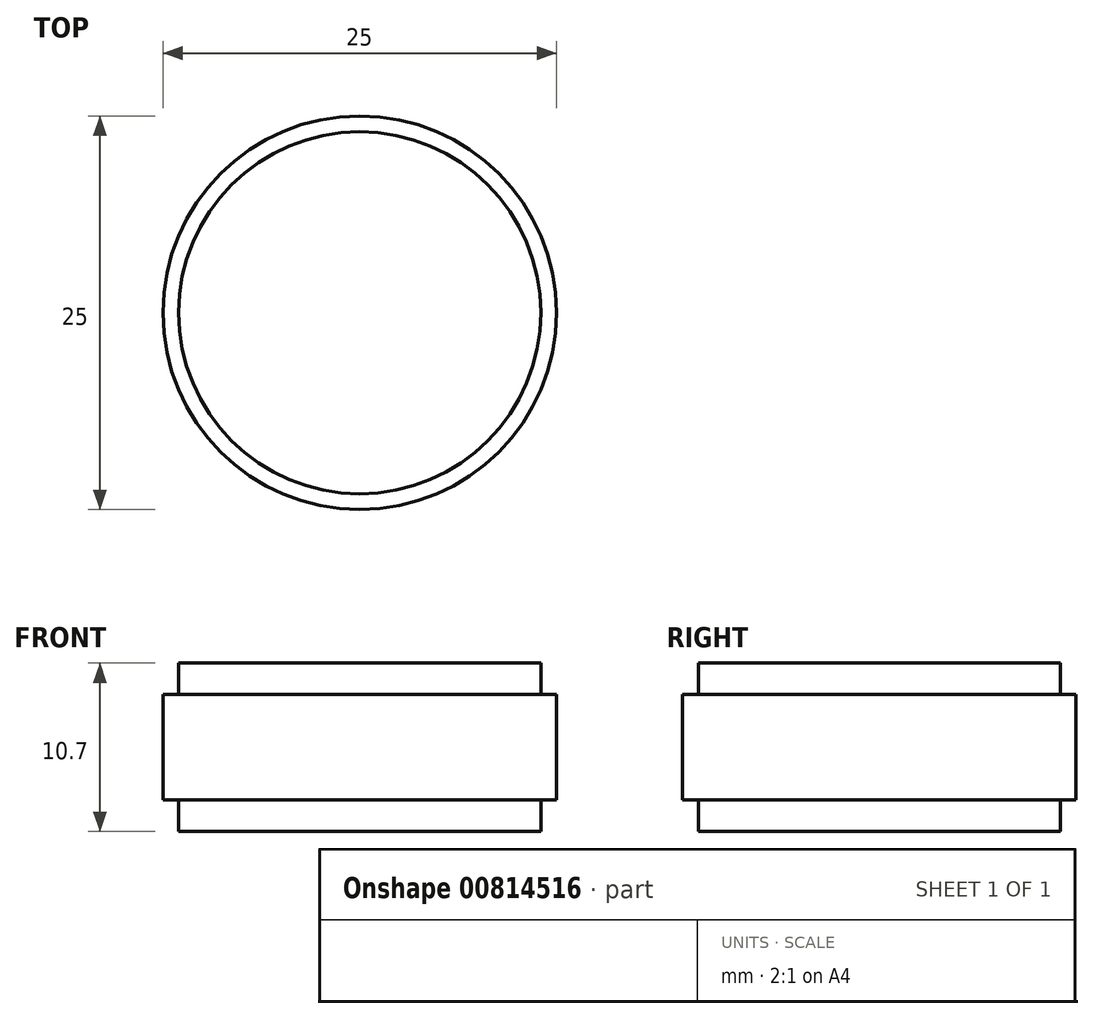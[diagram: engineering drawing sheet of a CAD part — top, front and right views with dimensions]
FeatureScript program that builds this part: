
annotation { "Feature Type Name" : "Feature", "Feature Type Description" : "" }
export const myFeature = defineFeature(function(context is Context, id is Id, definition is map)
    precondition{}
    {
        {
            var Q0;
            Q0=qCreatedBy(makeId("Top.planeOp"),FACE);
            var sketch = newSketch(context, id + "F0", { "sketchPlane" : qUnion([Q0])});
            skCircle(sketch, "E0", {"center": v(0, 0) * mm, "radius": 12.5 * mm});
            skSolve(sketch);
        }
        {
            var Q0;
            Q0=makeQuery(id+"F0.imprint","IMPRINT",FACE,{"disambiguationData":[TD([[makeQuery(id+"F0.imprint","IMPRINT",EDGE,{"derivedFrom":sQuery(id+"F0.wireOp",EDGE,"E0")}),1.0]])]});
            extrude(context, id + "F1", {"entities" : qUnion([Q0]), "depth" : 6.7 * mm, "offsetDistance" : 25.4 * mm});
        }
        {
            var Q0;
            Q0=makeQuery(id+"F1.opExtrude","CAP_FACE",FACE,{"disambiguationData":[OSD([sQuery(id+"F0.wireOp",EDGE,"E0")])],"isStart":false});
            var sketch = newSketch(context, id + "F2", { "sketchPlane" : qUnion([Q0])});
            skCircle(sketch, "E1", {"center": v(0, 0) * mm, "radius": 11.5 * mm});
            skSolve(sketch);
        }
        {
            var Q0;
            Q0 = qSketchRegion(id + "F2", true);
            extrude(context, id + "F3", {"entities" : qUnion([Q0]), "operationType" : NewBodyOperationType.ADD, "depth" : 2 * mm, "offsetDistance" : 25.4 * mm});
        }
        {
            var Q0;
            Q0=makeQuery(id+"F1.opExtrude","CAP_FACE",FACE,{"disambiguationData":[OSD([sQuery(id+"F0.wireOp",EDGE,"E0")])],"isStart":true});
            var sketch = newSketch(context, id + "F4", { "sketchPlane" : qUnion([Q0])});
            skCircle(sketch, "E2", {"center": v(0, 0) * mm, "radius": 11.5 * mm});
            skSolve(sketch);
        }
        {
            var Q0;
            Q0 = qSketchRegion(id + "F4", true);
            extrude(context, id + "F5", {"entities" : qUnion([Q0]), "operationType" : NewBodyOperationType.ADD, "depth" : 2 * mm, "offsetDistance" : 25.4 * mm});
        }
    });
